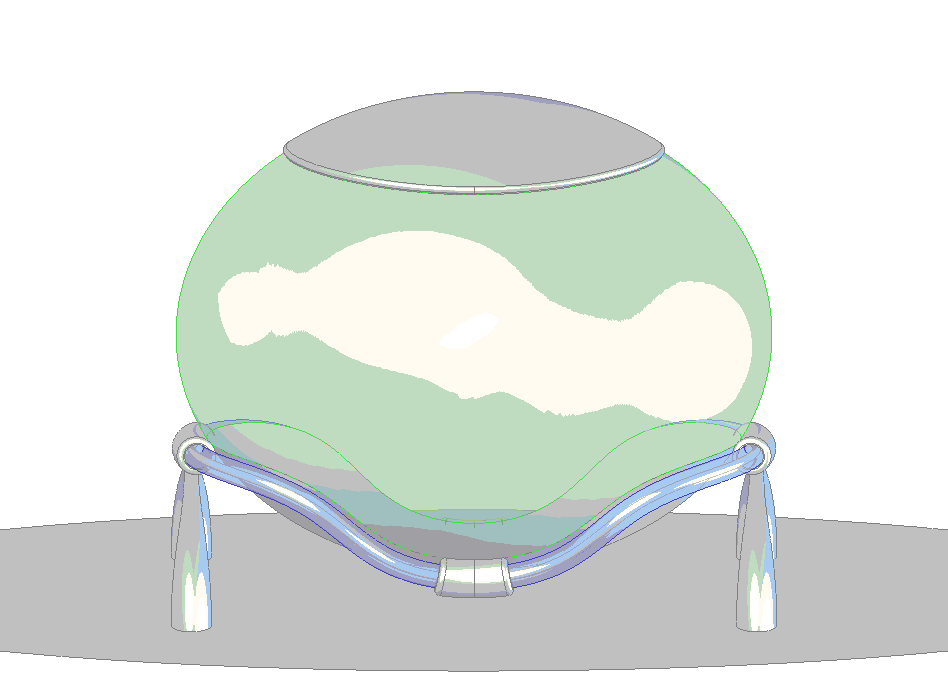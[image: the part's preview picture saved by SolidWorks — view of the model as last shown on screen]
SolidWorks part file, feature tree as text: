
SOLIDWORKS PART (.sldprt)
format: sldprt  version: not decoded by parser v0  size: 754,688 bytes
history: native  units: mm
features: sketch x9, fillet x5, sweep x3, mirror x3, plane x2, material x1 (+13 scaffold rows collapsed)
feature tree (36):
  scaffold x13  (default folders/planes/origin — collapsed)
  material  "Material <not specified>"
  sketch  "Sketch1"  dims[c1.D1=190.5mm c2.D1=360.0deg]
  sketch  "Sketch2"  dims[c1.PW2_UID_val=0.0deg c2.PW2_UID_val=0.0deg c3.PW2_UID_val=0.0deg c4.PW2_UID_val=0.0deg c5.PW2_UID_val=0.0deg]
  plane  "Plane1"
  sketch  "Sketch3"  dims[D1=7.62mm D2=2.54mm]
  sweep  "Sweep1"  PW2_UID_val=0deg
  sketch  "Sketch4"  dims[D1=2.159mm]
  fillet  "Fillet1"  Radius=1.778mm
  fillet  "Fillet2"  Radius=1.778mm
  plane  "Plane2"  Offset=83.134601mm
  sketch  "Sketch6"  dims[D1=4.572mm]
  sketch  "Sketch5"
  mirror  "Mirror1"
  mirror  "Mirror2"  PW2_UID_val=0deg
  sketch  "Sketch7"
  sweep  "Thicken2"
  fillet  "Fillet3"  Radius=1.778mm
  fillet  "Fillet4"  Radius=1.778mm
  mirror  "Mirror3"  PW2_UID_val=0deg
  sketch  "Sketch8"  dims[D1=0.0mm]
  sweep  "Thicken3"  PW2_UID_val=0deg
  fillet  "Fillet5"  Radius=1.524mm PW2_UID_val=0deg
  sketch  "Sketch10"  dims[PW2_UID_val=0.0deg]
decode coverage: 16 of 20 modeling features carry decoded parameters
note: suppression state not decoded; provenance and decode notes live in map.json
